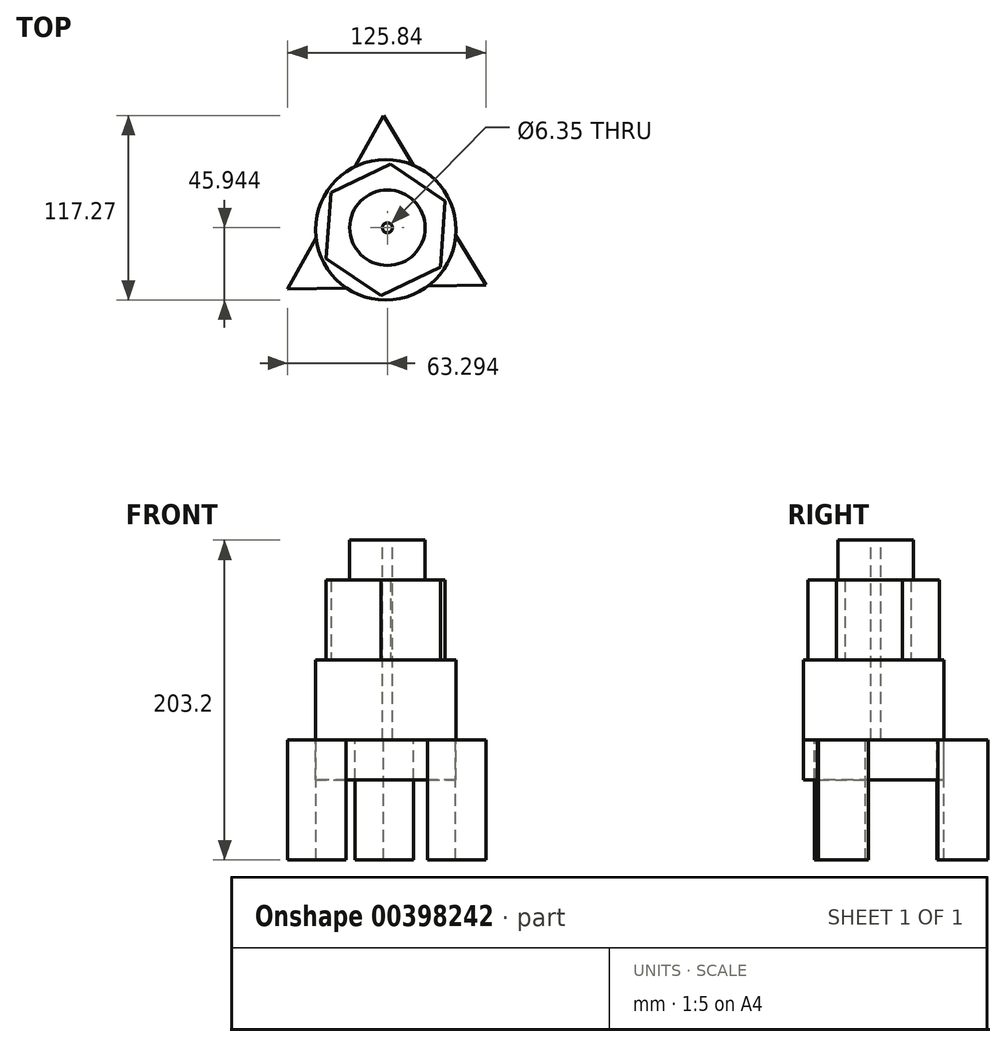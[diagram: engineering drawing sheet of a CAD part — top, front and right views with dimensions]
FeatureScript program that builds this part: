
annotation { "Feature Type Name" : "Feature", "Feature Type Description" : "" }
export const myFeature = defineFeature(function(context is Context, id is Id, definition is map)
    precondition{}
    {
        {
            var Q0;
            Q0=qCreatedBy(makeId("Top.planeOp"),FACE);
            var sketch = newSketch(context, id + "F0", { "sketchPlane" : qUnion([Q0])});
            skCircle(sketch, "E0", {"center": v(7.64, 21.56) * mm, "radius": 44.61 * mm});
            skSolve(sketch);
        }
        {
            var Q0;
            Q0=makeQuery(id+"F0.imprint","IMPRINT",FACE,{"disambiguationData":[TD([[makeQuery(id+"F0.imprint","IMPRINT",EDGE,{"derivedFrom":sQuery(id+"F0.wireOp",EDGE,"E0")}),1.0]])]});
            extrude(context, id + "F1", {"entities" : qUnion([Q0]), "depth" : 50.8 * mm});
        }
        {
            var Q0;
            Q0=makeQuery(id+"F1.opExtrude","CAP_FACE",FACE,{"disambiguationData":[OSD([sQuery(id+"F0.wireOp",EDGE,"E0")])],"isStart":false});
            var sketch = newSketch(context, id + "F2", { "sketchPlane" : qUnion([Q0])});
            skCircle(sketch, "E1.cCircle", {"center": v(7.64, 21.56) * mm, "radius": 36.33 * mm, "construction": true});
            skLineSegment(sketch, "E1.0", {"start": v(-27.1, 45.1) * mm, "end": v(10.65, 63.41) * mm});
            skLineSegment(sketch, "E1.1", {"start": v(10.65, 63.41) * mm, "end": v(45.38, 39.88) * mm});
            skLineSegment(sketch, "E1.2", {"start": v(45.38, 39.88) * mm, "end": v(42.37, -1.97) * mm});
            skLineSegment(sketch, "E1.3", {"start": v(42.37, -1.97) * mm, "end": v(4.62, -20.28) * mm});
            skLineSegment(sketch, "E1.4", {"start": v(4.62, -20.28) * mm, "end": v(-30.11, 3.25) * mm});
            skLineSegment(sketch, "E1.5", {"start": v(-30.11, 3.25) * mm, "end": v(-27.1, 45.1) * mm});
            skPoint(sketch, "E1.0.midPoint", {"position": v(-8.22, 54.25) * mm});
            skSolve(sketch);
        }
        {
            var Q0;
            Q0=makeQuery(id+"F2.imprint","IMPRINT",FACE,{"disambiguationData":[TD([[makeQuery(id+"F2.imprint","IMPRINT",EDGE,{"derivedFrom":sQuery(id+"F2.wireOp",EDGE,"E1.0")}),-1.0]])]});
            extrude(context, id + "F3", {"entities" : qUnion([Q0]), "operationType" : NewBodyOperationType.ADD, "depth" : 50.8 * mm});
        }
        {
            var Q0;
            Q0=makeQuery(id+"F1.opExtrude","CAP_FACE",FACE,{"disambiguationData":[OSD([sQuery(id+"F0.wireOp",EDGE,"E0")])],"isStart":true});
            var sketch = newSketch(context, id + "F4", { "sketchPlane" : qUnion([Q0])});
            skCircle(sketch, "E2.cCircle", {"center": v(7.64, -21.56) * mm, "radius": 36.33 * mm, "construction": true});
            skLineSegment(sketch, "E2.0", {"start": v(6.18, -94.22) * mm, "end": v(-54.56, 16.02) * mm});
            skLineSegment(sketch, "E2.1", {"start": v(-54.56, 16.02) * mm, "end": v(71.28, 13.5) * mm});
            skLineSegment(sketch, "E2.2", {"start": v(71.28, 13.5) * mm, "end": v(6.18, -94.22) * mm});
            skPoint(sketch, "E2.0.midPoint", {"position": v(-24.19, -39.1) * mm});
            skSolve(sketch);
        }
        {
            var Q0;
            {var subQ0=sQuery(id+"F4.wireOp",EDGE,"E2.1");var subQ1=sQuery(id+"F4.wireOp",EDGE,"E2.0");var subQ2=makeQuery(id+"F4.imprint","INTERSECT",VERTEX,{"derivedFrom":[subQ1,subQ0]});Q0=makeQuery(id+"F4.imprint","IMPRINT",FACE,{"disambiguationData":[TD([[makeQuery(id+"F4.imprint","IMPRINT",EDGE,{"disambiguationData":[TD([[subQ2,1.0]])],"derivedFrom":subQ1}),-1.0]])]});}
            var Q1;
            {var subQ0=sQuery(id+"F4.wireOp",EDGE,"E2.2");var subQ1=sQuery(id+"F4.wireOp",EDGE,"E2.1");var subQ2=makeQuery(id+"F4.imprint","INTERSECT",VERTEX,{"derivedFrom":[subQ1,subQ0]});Q1=makeQuery(id+"F4.imprint","IMPRINT",FACE,{"disambiguationData":[TD([[makeQuery(id+"F4.imprint","IMPRINT",EDGE,{"disambiguationData":[TD([[subQ2,1.0]])],"derivedFrom":subQ1}),-1.0]])]});}
            var Q2;
            {var subQ0=sQuery(id+"F4.wireOp",EDGE,"E2.2");var subQ1=sQuery(id+"F4.wireOp",EDGE,"E2.0");var subQ2=makeQuery(id+"F4.imprint","INTERSECT",VERTEX,{"derivedFrom":[subQ1,subQ0]});Q2=makeQuery(id+"F4.imprint","IMPRINT",FACE,{"disambiguationData":[TD([[makeQuery(id+"F4.imprint","IMPRINT",EDGE,{"disambiguationData":[TD([[subQ2,-1.0]])],"derivedFrom":subQ1}),-1.0]])]});}
            extrude(context, id + "F5", {"entities" : qUnion([Q0, Q1, Q2]), "depth" : 76.2 * mm});
        }
        {
            var Q0;
            Q0=makeQuery(id+"F1.opExtrude","CAP_FACE",FACE,{"disambiguationData":[OSD([sQuery(id+"F0.wireOp",EDGE,"E0")])],"isStart":true});
            extrude(context, id + "F6", {"entities" : qUnion([Q0]), "depth" : 25.4 * mm});
        }
        {
            var Q0;
            Q0=makeQuery(id+"F3.opExtrude","CAP_FACE",FACE,{"disambiguationData":[OSD([sQuery(id+"F2.wireOp",EDGE,"E1.0"),sQuery(id+"F2.wireOp",EDGE,"E1.1"),sQuery(id+"F2.wireOp",EDGE,"E1.2"),sQuery(id+"F2.wireOp",EDGE,"E1.3"),sQuery(id+"F2.wireOp",EDGE,"E1.4"),sQuery(id+"F2.wireOp",EDGE,"E1.5")])],"isStart":false});
            var sketch = newSketch(context, id + "F7", { "sketchPlane" : qUnion([Q0])});
            skCircle(sketch, "E3", {"center": v(8.73, 22.9) * mm, "radius": 23.94 * mm});
            skSolve(sketch);
        }
        {
            var Q0;
            Q0=makeQuery(id+"F7.imprint","IMPRINT",FACE,{"disambiguationData":[TD([[makeQuery(id+"F7.imprint","IMPRINT",EDGE,{"derivedFrom":sQuery(id+"F7.wireOp",EDGE,"E3")}),1.0]])]});
            extrude(context, id + "F8", {"entities" : qUnion([Q0]), "operationType" : NewBodyOperationType.ADD, "depth" : 25.4 * mm});
        }
        {
            var Q0;
            Q0=qCreatedBy(makeId("Front.planeOp"),FACE);
            cPlane(context, id + "F9", {"entities" : qUnion([Q0]), "cplaneType" : CPlaneType.OFFSET, "offset" : 25.15 * mm, "oppositeDirection" : true, "width" : 152.4 * mm, "height" : 152.4 * mm});
        }
        {
            var Q0;
            Q0=makeQuery(id+"F8.opExtrude","CAP_FACE",FACE,{"disambiguationData":[OSD([sQuery(id+"F7.wireOp",EDGE,"E3")])],"isStart":false});
            var sketch = newSketch(context, id + "F10", { "sketchPlane" : qUnion([Q0])});
            skPoint(sketch, "E4", {"position": v(8.73, 22.9) * mm});
            skSolve(sketch);
        }
        {
            var Q0;
            Q0=sQuery(id+"F10.wireOp",VERTEX,"E4");
            var Q1;
            Q1=makeQuery(id+"F1.opExtrude","SWEPT_BODY",BODY,{"disambiguationData":[OSD([sQuery(id+"F0.wireOp",EDGE,"E0")])]});
            hole(context, id + "F11", {"style" : HoleStyle.SIMPLE, "endStyle" : HoleEndStyle.THROUGH, "holeDiameter" : 6.35 * mm, "isTappedThrough" : true, "tappedDepth" : 12.7 * mm, "tapClearance" : 3, "locations" : qUnion([Q0]), "scope" : qUnion([Q1])});
        }
    });
